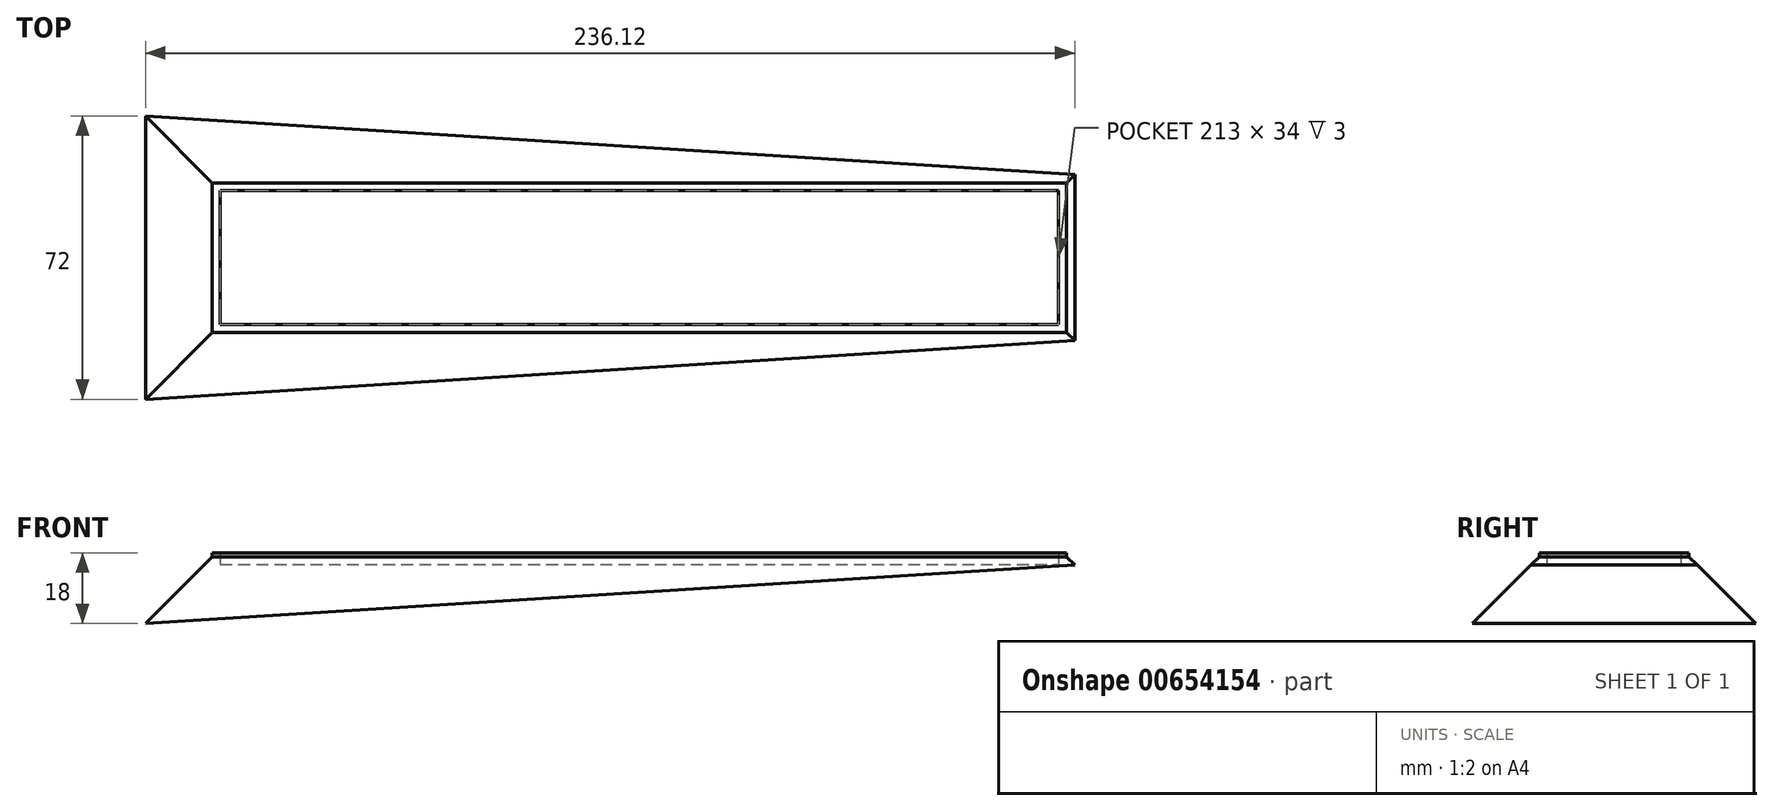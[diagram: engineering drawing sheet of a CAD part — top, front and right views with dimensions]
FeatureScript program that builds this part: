
annotation { "Feature Type Name" : "Feature", "Feature Type Description" : "" }
export const myFeature = defineFeature(function(context is Context, id is Id, definition is map)
    precondition{}
    {
        {
            var Q0;
            Q0=qCreatedBy(makeId("Top.planeOp"),FACE);
            var sketch = newSketch(context, id + "F0", { "sketchPlane" : qUnion([Q0])});
            skLineSegment(sketch, "E0.bottom", {"start": v(0, 0) * mm, "end": v(213, 0) * mm});
            skLineSegment(sketch, "E0.top", {"start": v(0, 34) * mm, "end": v(213, 34) * mm});
            skLineSegment(sketch, "E0.left", {"start": v(0, 0) * mm, "end": v(0, 34) * mm});
            skLineSegment(sketch, "E0.right", {"start": v(213, 0) * mm, "end": v(213, 34) * mm});
            skLineSegment(sketch, "E1.0", {"start": v(-2, 36) * mm, "end": v(215, 36) * mm});
            skLineSegment(sketch, "E1.1", {"start": v(-2, -2) * mm, "end": v(-2, 36) * mm});
            skLineSegment(sketch, "E1.2", {"start": v(-2, -2) * mm, "end": v(215, -2) * mm});
            skLineSegment(sketch, "E1.3", {"start": v(215, -2) * mm, "end": v(215, 36) * mm});
            skSolve(sketch);
        }
        {
            var Q0;
            Q0=makeQuery(id+"F0.imprint","IMPRINT",FACE,{"disambiguationData":[TD([[makeQuery(id+"F0.imprint","IMPRINT",EDGE,{"derivedFrom":sQuery(id+"F0.wireOp",EDGE,"E0.bottom")}),-1.0]])]});
            extrude(context, id + "F1", {"entities" : qUnion([Q0]), "depth" : 1 * mm, "offsetDistance" : 25 * mm});
        }
        {
            var Q0;
            Q0=makeQuery(id+"F0.imprint","IMPRINT",FACE,{"disambiguationData":[TD([[makeQuery(id+"F0.imprint","IMPRINT",EDGE,{"derivedFrom":sQuery(id+"F0.wireOp",EDGE,"E0.bottom")}),1.0]])]});
            var Q1;
            Q1=makeQuery(id+"F0.imprint","IMPRINT",FACE,{"disambiguationData":[TD([[makeQuery(id+"F0.imprint","IMPRINT",EDGE,{"derivedFrom":sQuery(id+"F0.wireOp",EDGE,"E0.bottom")}),-1.0]])]});
            extrude(context, id + "F2", {"entities" : qUnion([Q0, Q1]), "operationType" : NewBodyOperationType.ADD, "oppositeDirection" : true, "depth" : 17 * mm, "offsetDistance" : 25 * mm, "hasDraft" : true, "draftAngle" : 45 * degree});
        }
        {
            var Q0;
            Q0=makeQuery(id+"F0.imprint","IMPRINT",FACE,{"disambiguationData":[TD([[makeQuery(id+"F0.imprint","IMPRINT",EDGE,{"derivedFrom":sQuery(id+"F0.wireOp",EDGE,"E0.bottom")}),1.0]])]});
            extrude(context, id + "F3", {"entities" : qUnion([Q0]), "operationType" : NewBodyOperationType.REMOVE, "oppositeDirection" : true, "depth" : 2 * mm, "offsetDistance" : 25 * mm});
        }
        {
            var Q0;
            Q0=qCreatedBy(makeId("Front.planeOp"),FACE);
            var sketch = newSketch(context, id + "F4", { "sketchPlane" : qUnion([Q0])});
            skLineSegment(sketch, "E2", {"start": v(-19, -17) * mm, "end": v(217.12, -2.12) * mm});
            skLineSegment(sketch, "E3", {"start": v(217.12, -2.12) * mm, "end": v(234.95, -19.95) * mm});
            skLineSegment(sketch, "E4", {"start": v(234.95, -19.95) * mm, "end": v(-19, -17) * mm});
            skSolve(sketch);
        }
        {
            var Q0;
            Q0 = qSketchRegion(id + "F4", true);
            extrude(context, id + "F5", {"entities" : qUnion([Q0]), "operationType" : NewBodyOperationType.REMOVE, "endBound" : BoundingType.THROUGH_ALL, "oppositeDirection" : true, "depth" : 25 * mm, "offsetDistance" : 25 * mm, "hasSecondDirection" : true, "secondDirectionOppositeDirection" : false, "secondDirectionDepth" : 25 * mm});
        }
    });
